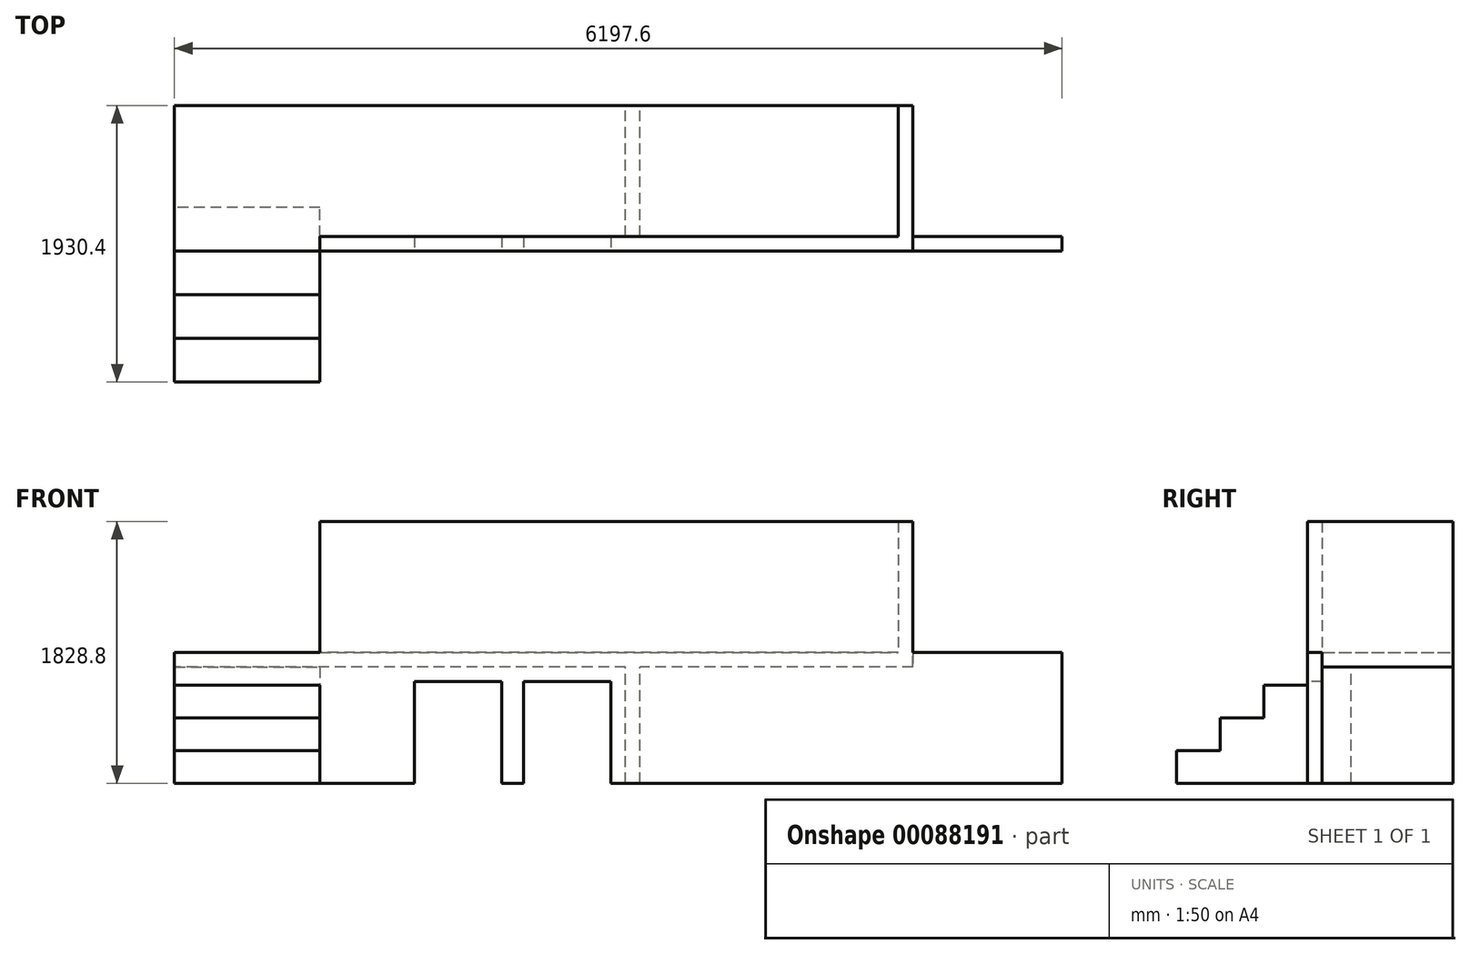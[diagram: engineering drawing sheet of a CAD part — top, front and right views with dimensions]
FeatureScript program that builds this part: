
annotation { "Feature Type Name" : "Feature", "Feature Type Description" : "" }
export const myFeature = defineFeature(function(context is Context, id is Id, definition is map)
    precondition{}
    {
        {
            var Q0;
            Q0=qCreatedBy(makeId("Top.planeOp"),FACE);
            var sketch = newSketch(context, id + "F0", { "sketchPlane" : qUnion([Q0])});
            skLineSegment(sketch, "E0.bottom", {"start": v(2578.1, -508) * mm, "end": v(-2578.1, -508) * mm});
            skLineSegment(sketch, "E0.top", {"start": v(2578.1, 508) * mm, "end": v(-2578.1, 508) * mm});
            skLineSegment(sketch, "E0.left", {"start": v(2578.1, -508) * mm, "end": v(2578.1, 508) * mm});
            skLineSegment(sketch, "E0.right", {"start": v(-2578.1, -508) * mm, "end": v(-2578.1, 508) * mm});
            skPoint(sketch, "E0.middle", {"position": v(0, 0) * mm});
            skSolve(sketch);
        }
        {
            var Q0;
            Q0=qSketchRegion(id+"F0",true);
            extrude(context, id + "F1", {"entities" : qUnion([Q0]), "oppositeDirection" : true, "depth" : 101.6 * mm});
        }
        {
            var Q0;
            Q0=makeQuery(id+"F1.opExtrude","SWEPT_FACE",FACE,{"disambiguationData":[OSD([sQuery(id+"F0.wireOp",EDGE,"E0.right")])]});
            var sketch = newSketch(context, id + "F2", { "sketchPlane" : qUnion([Q0])});
            skLineSegment(sketch, "E1", {"start": v(508, 0) * mm, "end": v(508, -228.6) * mm});
            skLineSegment(sketch, "E2", {"start": v(508, -228.6) * mm, "end": v(812.8, -228.6) * mm});
            skLineSegment(sketch, "E3", {"start": v(812.8, -228.6) * mm, "end": v(812.8, -457.2) * mm});
            skLineSegment(sketch, "E4", {"start": v(812.8, -457.2) * mm, "end": v(1117.6, -457.2) * mm});
            skLineSegment(sketch, "E5", {"start": v(1117.6, -457.2) * mm, "end": v(1117.6, -685.8) * mm});
            skLineSegment(sketch, "E6", {"start": v(1117.6, -685.8) * mm, "end": v(1422.4, -685.8) * mm});
            skLineSegment(sketch, "E7", {"start": v(1422.4, -685.8) * mm, "end": v(1422.4, -914.4) * mm});
            skLineSegment(sketch, "E8", {"start": v(1422.4, -914.4) * mm, "end": v(203.2, -914.4) * mm});
            skLineSegment(sketch, "E9", {"start": v(203.2, -914.4) * mm, "end": v(203.2, 0) * mm});
            skLineSegment(sketch, "E10", {"start": v(203.2, 0) * mm, "end": v(508, 0) * mm});
            skSolve(sketch);
        }
        {
            var Q0;
            Q0=qSketchRegion(id+"F2",true);
            extrude(context, id + "F3", {"entities" : qUnion([Q0]), "operationType" : NewBodyOperationType.ADD, "oppositeDirection" : true, "depth" : 1016 * mm});
        }
        {
            var Q0;
            Q0=makeQuery(id+"F3.boolean.opBoolean","MERGE",FACE,{"derivedFrom":[makeQuery(id+"F1.opExtrude","SWEPT_FACE",FACE,{"disambiguationData":[OSD([sQuery(id+"F0.wireOp",EDGE,"E0.bottom")])]}),makeQuery(id+"F3.opExtrude","SWEPT_FACE",FACE,{"disambiguationData":[OSD([sQuery(id+"F2.wireOp",EDGE,"E1")])]})]});
            var sketch = newSketch(context, id + "F4", { "sketchPlane" : qUnion([Q0])});
            skLineSegment(sketch, "E11.0", {"start": v(-1562.1, -101.6) * mm, "end": v(-1562.1, -228.6) * mm});
            skLineSegment(sketch, "E12", {"start": v(-1562.1, -101.6) * mm, "end": v(723.9, -101.6) * mm});
            skLineSegment(sketch, "E13", {"start": v(723.9, -101.6) * mm, "end": v(723.9, -914.4) * mm});
            skLineSegment(sketch, "E14", {"start": v(723.9, -914.4) * mm, "end": v(-1562.1, -914.4) * mm});
            skLineSegment(sketch, "E15", {"start": v(-1562.1, -228.6) * mm, "end": v(-1562.1, -914.4) * mm});
            skLineSegment(sketch, "E16.bottom", {"start": v(-901.7, -914.4) * mm, "end": v(-292.1, -914.4) * mm});
            skLineSegment(sketch, "E16.top", {"start": v(-901.7, -203.2) * mm, "end": v(-292.1, -203.2) * mm});
            skLineSegment(sketch, "E16.left", {"start": v(-901.7, -914.4) * mm, "end": v(-901.7, -203.2) * mm});
            skLineSegment(sketch, "E16.right", {"start": v(-292.1, -914.4) * mm, "end": v(-292.1, -203.2) * mm});
            skLineSegment(sketch, "E17.bottom", {"start": v(-139.7, -914.4) * mm, "end": v(469.9, -914.4) * mm});
            skLineSegment(sketch, "E17.top", {"start": v(-139.7, -203.2) * mm, "end": v(469.9, -203.2) * mm});
            skLineSegment(sketch, "E17.left", {"start": v(-139.7, -914.4) * mm, "end": v(-139.7, -203.2) * mm});
            skLineSegment(sketch, "E17.right", {"start": v(469.9, -914.4) * mm, "end": v(469.9, -203.2) * mm});
            skSolve(sketch);
        }
        {
            var Q0;
            Q0=makeQuery(id+"F4.imprint","IMPRINT",FACE,{"disambiguationData":[TD([[makeQuery(id+"F4.imprint","IMPRINT",EDGE,{"derivedFrom":sQuery(id+"F4.wireOp",EDGE,"E11.0")}),1.0]])]});
            extrude(context, id + "F5", {"entities" : qUnion([Q0]), "operationType" : NewBodyOperationType.ADD, "oppositeDirection" : true, "depth" : 101.6 * mm});
        }
        {
            var Q0;
            Q0=makeQuery(id+"F3.opExtrude","SWEPT_FACE",FACE,{"disambiguationData":[OSD([sQuery(id+"F2.wireOp",EDGE,"E2")])]});
            var sketch = newSketch(context, id + "F6", { "sketchPlane" : qUnion([Q0])});
            skLineSegment(sketch, "E18", {"start": v(-1562.1, -508) * mm, "end": v(-952.5, -508) * mm});
            skLineSegment(sketch, "E19", {"start": v(-1562.1, -1422.4) * mm, "end": v(-1562.1, -508) * mm});
            skLineSegment(sketch, "E20", {"start": v(-952.5, -508) * mm, "end": v(-1562.1, -1422.4) * mm});
            skSolve(sketch);
        }
        {
            var Q0;
            Q0=qSketchRegion(id+"F6",true);
            var Q1;
            {var subQ0=sQuery(id+"F4.wireOp",EDGE,"E14");Q1=makeQuery(id+"F5.boolean.opBoolean","MERGE",FACE,{"derivedFrom":[makeQuery(id+"F3.opExtrude","SWEPT_FACE",FACE,{"disambiguationData":[OSD([sQuery(id+"F2.wireOp",EDGE,"E8")])]}),makeQuery(id+"F5.opExtrude","SWEPT_FACE",FACE,{"disambiguationData":[OSD([subQ0]),TDD([makeQuery(id+"F4.imprint","IMPRINT",EDGE,{"disambiguationData":[TD([[makeQuery(id+"F4.imprint","INTERSECT",VERTEX,{"derivedFrom":[subQ0,sQuery(id+"F4.wireOp",EDGE,"E15")]}),1.0]])],"derivedFrom":subQ0})])]})]});}
            extrude(context, id + "F7", {"entities" : qUnion([Q0]), "operationType" : NewBodyOperationType.ADD, "endBound" : BoundingType.UP_TO_SURFACE, "oppositeDirection" : true, "endBoundEntityFace" : qUnion([Q1]), "depth" : 25.4 * mm});
        }
        {
            var Q0;
            Q0=makeQuery(id+"F7.boolean.opBoolean","MERGE",FACE,{"derivedFrom":[makeQuery(id+"F3.opExtrude","SWEPT_FACE",FACE,{"disambiguationData":[OSD([sQuery(id+"F2.wireOp",EDGE,"E2")])]}),makeQuery(id+"F7.opExtrude","CAP_FACE",FACE,{"disambiguationData":[OSD([sQuery(id+"F6.wireOp",EDGE,"E18"),sQuery(id+"F6.wireOp",EDGE,"E19"),sQuery(id+"F6.wireOp",EDGE,"E20")])],"isStart":true})]});
            var sketch = newSketch(context, id + "F8", { "sketchPlane" : qUnion([Q0])});
            skLineSegment(sketch, "E21.0", {"start": v(-1562.1, -812.8) * mm, "end": v(-1562.1, -1422.4) * mm});
            skLineSegment(sketch, "E21.1", {"start": v(-1155.7, -812.8) * mm, "end": v(-1562.1, -1422.4) * mm});
            skLineSegment(sketch, "E22", {"start": v(-1562.1, -812.8) * mm, "end": v(-1155.7, -812.8) * mm});
            skPoint(sketch, "E23.orphan", {"position": v(-952.5, -508) * mm});
            skSolve(sketch);
        }
        {
            var Q0;
            Q0=qSketchRegion(id+"F8",true);
            var Q1;
            Q1=makeQuery(id+"F3.opExtrude","SWEPT_FACE",FACE,{"disambiguationData":[OSD([sQuery(id+"F2.wireOp",EDGE,"E4")])]});
            extrude(context, id + "F9", {"entities" : qUnion([Q0]), "operationType" : NewBodyOperationType.REMOVE, "endBound" : BoundingType.UP_TO_SURFACE, "oppositeDirection" : true, "endBoundEntityFace" : qUnion([Q1]), "depth" : 25.4 * mm});
        }
        {
            var Q0;
            {var subQ0=sQuery(id+"F2.wireOp",EDGE,"E4");Q0=makeQuery(id+"F9.boolean.opBoolean","MERGE",FACE,{"derivedFrom":[makeQuery(id+"F3.opExtrude","SWEPT_FACE",FACE,{"disambiguationData":[OSD([subQ0])]}),makeQuery(id+"F9.opExtrude","CAP_FACE",FACE,{"disambiguationData":[OSD([subQ0])],"isStart":false})]});}
            var sketch = newSketch(context, id + "F10", { "sketchPlane" : qUnion([Q0])});
            skLineSegment(sketch, "E24.0", {"start": v(-1562.1, -1117.6) * mm, "end": v(-1562.1, -1422.4) * mm});
            skLineSegment(sketch, "E24.1", {"start": v(-1358.9, -1117.6) * mm, "end": v(-1562.1, -1422.4) * mm});
            skLineSegment(sketch, "E25", {"start": v(-1562.1, -1117.6) * mm, "end": v(-1358.9, -1117.6) * mm});
            skPoint(sketch, "E26.orphan", {"position": v(-1155.7, -812.8) * mm});
            skSolve(sketch);
        }
        {
            var Q0;
            Q0=qSketchRegion(id+"F10",true);
            var Q1;
            Q1=makeQuery(id+"F3.opExtrude","SWEPT_FACE",FACE,{"disambiguationData":[OSD([sQuery(id+"F2.wireOp",EDGE,"E6")])]});
            extrude(context, id + "F11", {"entities" : qUnion([Q0]), "operationType" : NewBodyOperationType.REMOVE, "endBound" : BoundingType.UP_TO_SURFACE, "oppositeDirection" : true, "endBoundEntityFace" : qUnion([Q1]), "depth" : 25.4 * mm});
        }
        {
            var Q0;
            Q0=makeQuery(id+"F1.opExtrude","CAP_FACE",FACE,{"disambiguationData":[OSD([sQuery(id+"F0.wireOp",EDGE,"E0.bottom"),sQuery(id+"F0.wireOp",EDGE,"E0.top"),sQuery(id+"F0.wireOp",EDGE,"E0.left"),sQuery(id+"F0.wireOp",EDGE,"E0.right")])],"isStart":true});
            var sketch = newSketch(context, id + "F12", { "sketchPlane" : qUnion([Q0])});
            skLineSegment(sketch, "E27.bottom", {"start": v(-952.5, -508) * mm, "end": v(2578.1, -508) * mm});
            skLineSegment(sketch, "E27.top", {"start": v(-952.5, -406.4) * mm, "end": v(2476.5, -406.4) * mm});
            skLineSegment(sketch, "E27.left", {"start": v(-952.5, -508) * mm, "end": v(-952.5, -406.4) * mm});
            skLineSegment(sketch, "E27.right", {"start": v(2578.1, -508) * mm, "end": v(2578.1, -406.4) * mm});
            skLineSegment(sketch, "E28.top", {"start": v(2578.1, 508) * mm, "end": v(2476.5, 508) * mm});
            skLineSegment(sketch, "E28.left", {"start": v(2578.1, -508) * mm, "end": v(2578.1, 508) * mm});
            skLineSegment(sketch, "E28.right", {"start": v(2476.5, -406.4) * mm, "end": v(2476.5, 508) * mm});
            skSolve(sketch);
        }
        {
            var Q0;
            Q0=qSketchRegion(id+"F12",true);
            extrude(context, id + "F13", {"entities" : qUnion([Q0]), "operationType" : NewBodyOperationType.ADD, "depth" : 914.4 * mm});
        }
        {
            var Q0;
            Q0=makeQuery(id+"F1.opExtrude","CAP_FACE",FACE,{"disambiguationData":[OSD([sQuery(id+"F0.wireOp",EDGE,"E0.bottom"),sQuery(id+"F0.wireOp",EDGE,"E0.top"),sQuery(id+"F0.wireOp",EDGE,"E0.left"),sQuery(id+"F0.wireOp",EDGE,"E0.right")])],"isStart":false});
            var sketch = newSketch(context, id + "F14", { "sketchPlane" : qUnion([Q0])});
            skLineSegment(sketch, "E29.bottom", {"start": v(673.1, 406.4) * mm, "end": v(571.5, 406.4) * mm});
            skLineSegment(sketch, "E29.top", {"start": v(673.1, -508) * mm, "end": v(571.5, -508) * mm});
            skLineSegment(sketch, "E29.left", {"start": v(673.1, 406.4) * mm, "end": v(673.1, -508) * mm});
            skLineSegment(sketch, "E29.right", {"start": v(571.5, 406.4) * mm, "end": v(571.5, -508) * mm});
            skSolve(sketch);
        }
        {
            var Q0;
            Q0=qSketchRegion(id+"F14",true);
            var Q1;
            {var subQ0=sQuery(id+"F4.wireOp",EDGE,"E14");Q1=makeQuery(id+"F5.opExtrude","SWEPT_FACE",FACE,{"disambiguationData":[OSD([subQ0]),TDD([makeQuery(id+"F4.imprint","IMPRINT",EDGE,{"disambiguationData":[TD([[makeQuery(id+"F4.imprint","INTERSECT",VERTEX,{"derivedFrom":[sQuery(id+"F4.wireOp",EDGE,"E13"),subQ0]}),-1.0]])],"derivedFrom":subQ0})])]});}
            extrude(context, id + "F15", {"entities" : qUnion([Q0]), "operationType" : NewBodyOperationType.ADD, "endBound" : BoundingType.UP_TO_SURFACE, "endBoundEntityFace" : qUnion([Q1]), "depth" : 25.4 * mm});
        }
        {
            var Q0;
            Q0=makeQuery(id+"F13.boolean.opBoolean","MERGE",FACE,{"derivedFrom":[makeQuery(id+"F5.boolean.opBoolean","MERGE",FACE,{"derivedFrom":[makeQuery(id+"F3.boolean.opBoolean","MERGE",FACE,{"derivedFrom":[makeQuery(id+"F1.opExtrude","SWEPT_FACE",FACE,{"disambiguationData":[OSD([sQuery(id+"F0.wireOp",EDGE,"E0.bottom")])]}),makeQuery(id+"F3.opExtrude","SWEPT_FACE",FACE,{"disambiguationData":[OSD([sQuery(id+"F2.wireOp",EDGE,"E1")])]})]}),makeQuery(id+"F5.opExtrude","CAP_FACE",FACE,{"disambiguationData":[OSD([sQuery(id+"F4.wireOp",EDGE,"E11.0"),sQuery(id+"F4.wireOp",EDGE,"E12"),sQuery(id+"F4.wireOp",EDGE,"E13"),sQuery(id+"F4.wireOp",EDGE,"E14"),sQuery(id+"F4.wireOp",EDGE,"E15"),sQuery(id+"F4.wireOp",EDGE,"E16.top"),sQuery(id+"F4.wireOp",EDGE,"E16.left"),sQuery(id+"F4.wireOp",EDGE,"E16.right"),sQuery(id+"F4.wireOp",EDGE,"E17.top"),sQuery(id+"F4.wireOp",EDGE,"E17.left"),sQuery(id+"F4.wireOp",EDGE,"E17.right")])],"isStart":true})]}),makeQuery(id+"F13.opExtrude","SWEPT_FACE",FACE,{"disambiguationData":[OSD([sQuery(id+"F12.wireOp",EDGE,"E27.bottom")])]})]});
            var sketch = newSketch(context, id + "F16", { "sketchPlane" : qUnion([Q0])});
            skLineSegment(sketch, "E30.bottom", {"start": v(723.9, 0) * mm, "end": v(3619.5, 0) * mm});
            skLineSegment(sketch, "E30.top", {"start": v(723.9, -914.4) * mm, "end": v(3619.5, -914.4) * mm});
            skLineSegment(sketch, "E30.left", {"start": v(723.9, 0) * mm, "end": v(723.9, -914.4) * mm});
            skLineSegment(sketch, "E30.right", {"start": v(3619.5, 0) * mm, "end": v(3619.5, -914.4) * mm});
            skSolve(sketch);
        }
        {
            var Q0;
            Q0=qSketchRegion(id+"F16",true);
            extrude(context, id + "F17", {"entities" : qUnion([Q0]), "operationType" : NewBodyOperationType.ADD, "oppositeDirection" : true, "depth" : 101.6 * mm});
        }
        {
            var Q0;
            Q0=makeQuery(id+"F1.opExtrude","CAP_FACE",FACE,{"disambiguationData":[OSD([sQuery(id+"F0.wireOp",EDGE,"E0.bottom"),sQuery(id+"F0.wireOp",EDGE,"E0.top"),sQuery(id+"F0.wireOp",EDGE,"E0.left"),sQuery(id+"F0.wireOp",EDGE,"E0.right")])],"isStart":true});
            var sketch = newSketch(context, id + "F18", { "sketchPlane" : qUnion([Q0])});
            skLineSegment(sketch, "E31.bottom", {"start": v(-1562.1, -1422.4) * mm, "end": v(-952.5, -1422.4) * mm});
            skLineSegment(sketch, "E31.top", {"start": v(-1562.1, -508) * mm, "end": v(-952.5, -508) * mm});
            skLineSegment(sketch, "E31.left", {"start": v(-1562.1, -1422.4) * mm, "end": v(-1562.1, -508) * mm});
            skLineSegment(sketch, "E31.right", {"start": v(-952.5, -1422.4) * mm, "end": v(-952.5, -508) * mm});
            skSolve(sketch);
        }
        {
            var Q0;
            Q0 = qSketchRegion(id + "F18", true);
            extrude(context, id + "F19", {"entities" : qUnion([Q0]), "operationType" : NewBodyOperationType.REMOVE, "endBound" : BoundingType.THROUGH_ALL, "oppositeDirection" : true, "depth" : 25.4 * mm});
        }
        {
            var Q0;
            Q0=makeQuery(id+"F1.opExtrude","CAP_FACE",FACE,{"disambiguationData":[OSD([sQuery(id+"F0.wireOp",EDGE,"E0.bottom"),sQuery(id+"F0.wireOp",EDGE,"E0.top"),sQuery(id+"F0.wireOp",EDGE,"E0.left"),sQuery(id+"F0.wireOp",EDGE,"E0.right")])],"isStart":true});
            var sketch = newSketch(context, id + "F20", { "sketchPlane" : qUnion([Q0])});
            skLineSegment(sketch, "E32.bottom", {"start": v(-952.5, -406.4) * mm, "end": v(-1562.1, -406.4) * mm});
            skLineSegment(sketch, "E32.top", {"start": v(-952.5, -508) * mm, "end": v(-1562.1, -508) * mm});
            skLineSegment(sketch, "E32.left", {"start": v(-952.5, -406.4) * mm, "end": v(-952.5, -508) * mm});
            skLineSegment(sketch, "E32.right", {"start": v(-1562.1, -406.4) * mm, "end": v(-1562.1, -508) * mm});
            skSolve(sketch);
        }
        {
            var Q0;
            Q0 = qSketchRegion(id + "F20", true);
            var Q1;
            Q1=makeQuery(id+"F13.opExtrude","CAP_FACE",FACE,{"disambiguationData":[OSD([sQuery(id+"F12.wireOp",EDGE,"E27.bottom"),sQuery(id+"F12.wireOp",EDGE,"E27.top"),sQuery(id+"F12.wireOp",EDGE,"E27.left"),sQuery(id+"F12.wireOp",EDGE,"E28.top"),sQuery(id+"F12.wireOp",EDGE,"E28.left"),sQuery(id+"F12.wireOp",EDGE,"E28.right")])],"isStart":false});
            extrude(context, id + "F21", {"entities" : qUnion([Q0]), "operationType" : NewBodyOperationType.ADD, "endBound" : BoundingType.UP_TO_SURFACE, "endBoundEntityFace" : qUnion([Q1]), "depth" : 25.4 * mm});
        }
    });
